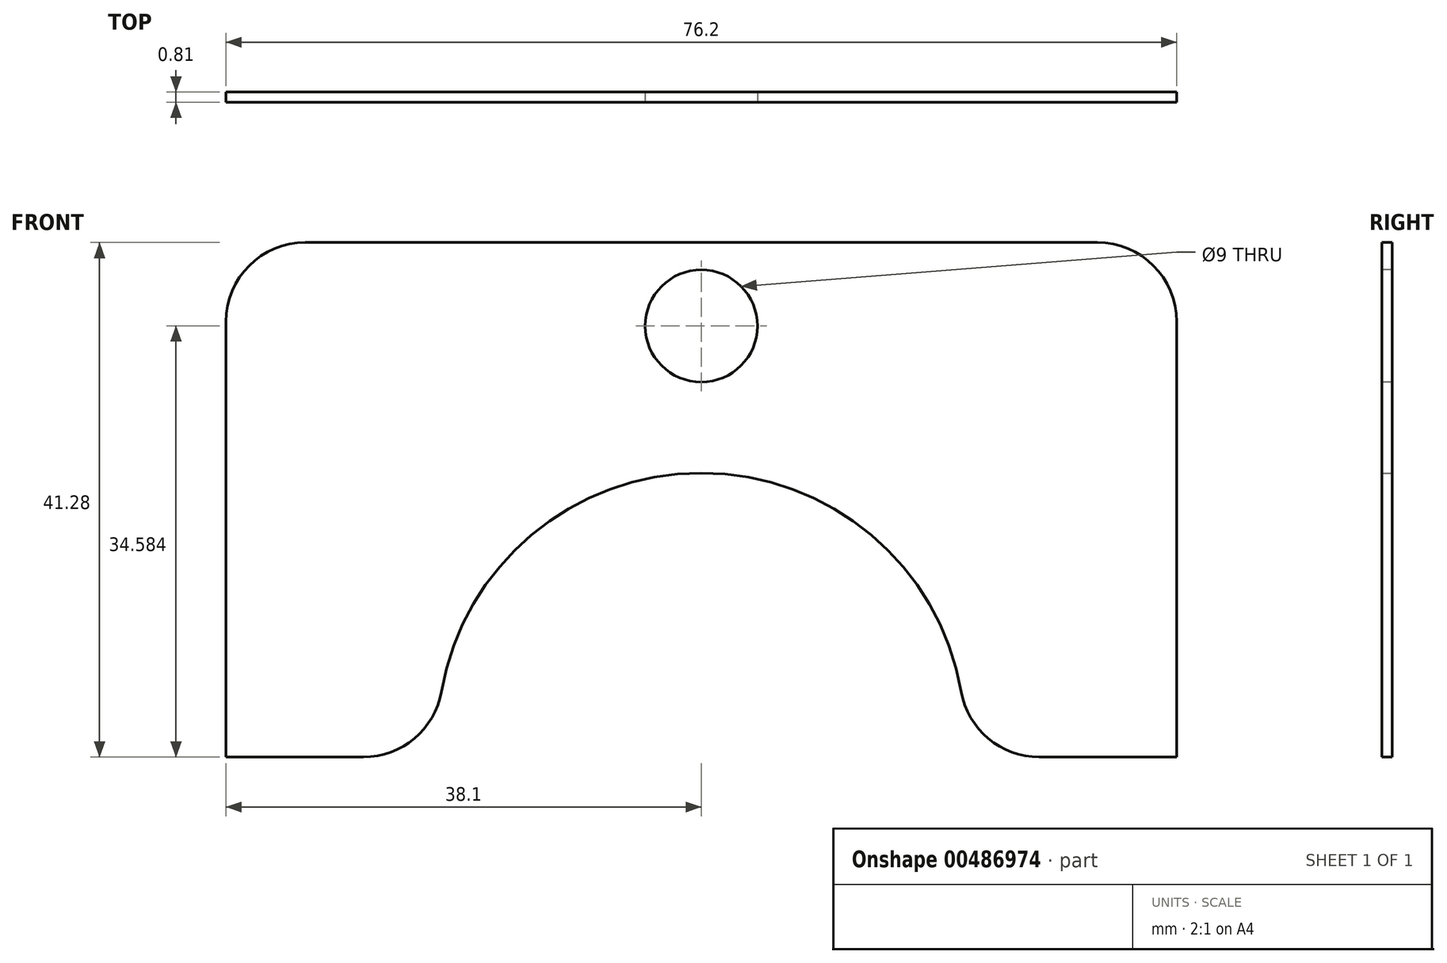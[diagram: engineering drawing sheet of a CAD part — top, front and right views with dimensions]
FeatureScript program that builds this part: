
annotation { "Feature Type Name" : "Feature", "Feature Type Description" : "" }
export const myFeature = defineFeature(function(context is Context, id is Id, definition is map)
    precondition{}
    {
        {
            var Q0;
            Q0=qCreatedBy(makeId("Front.planeOp"),FACE);
            var sketch = newSketch(context, id + "F0", { "sketchPlane" : qUnion([Q0])});
            skArc(sketch, "E0", {"start": v(20.83, 3.62) * mm, "mid": v(0, 21.15) * mm, "end": v(-20.83, 3.62) * mm});
            skLineSegment(sketch, "E1.bottom", {"start": v(-38.1, -1.64) * mm, "end": v(-27.09, -1.64) * mm});
            skLineSegment(sketch, "E1.top", {"start": v(-31.75, 39.64) * mm, "end": v(31.75, 39.64) * mm});
            skLineSegment(sketch, "E1.left", {"start": v(-38.1, -1.64) * mm, "end": v(-38.1, 33.29) * mm});
            skLineSegment(sketch, "E1.right", {"start": v(38.1, -1.64) * mm, "end": v(38.1, 33.29) * mm});
            skLineSegment(sketch, "E2.trimOffspring", {"start": v(27.09, -1.64) * mm, "end": v(38.1, -1.64) * mm});
            skPoint(sketch, "E3.visualSharp", {"position": v(21.08, -1.64) * mm});
            skArc(sketch, "E3.filletArc", {"start": v(20.83, 3.62) * mm, "mid": v(23, -0.15) * mm, "end": v(27.09, -1.64) * mm});
            skPoint(sketch, "E4.visualSharp", {"position": v(-21.08, -1.64) * mm});
            skArc(sketch, "E4.filletArc", {"start": v(-27.09, -1.64) * mm, "mid": v(-23, -0.15) * mm, "end": v(-20.83, 3.62) * mm});
            skPoint(sketch, "E5.visualSharp", {"position": v(-38.1, 39.64) * mm});
            skArc(sketch, "E5.filletArc", {"start": v(-31.75, 39.64) * mm, "mid": v(-36.24, 37.78) * mm, "end": v(-38.1, 33.29) * mm});
            skPoint(sketch, "E6.visualSharp", {"position": v(38.1, 39.64) * mm});
            skArc(sketch, "E6.filletArc", {"start": v(38.1, 33.29) * mm, "mid": v(36.24, 37.78) * mm, "end": v(31.75, 39.64) * mm});
            skSolve(sketch);
        }
        {
            var Q0;
            Q0=makeQuery(id+"F0.imprint","IMPRINT",FACE,{"disambiguationData":[TD([[makeQuery(id+"F0.imprint","IMPRINT",EDGE,{"derivedFrom":sQuery(id+"F0.wireOp",EDGE,"E0")}),-1.0]])]});
            extrude(context, id + "F1", {"entities" : qUnion([Q0]), "depth" : 0.81 * mm});
        }
        {
            var Q0;
            Q0=makeQuery(id+"F1.opExtrude","CAP_FACE",FACE,{"disambiguationData":[OSD([sQuery(id+"F0.wireOp",EDGE,"E0"),sQuery(id+"F0.wireOp",EDGE,"E1.bottom"),sQuery(id+"F0.wireOp",EDGE,"E1.top"),sQuery(id+"F0.wireOp",EDGE,"E1.left"),sQuery(id+"F0.wireOp",EDGE,"E1.right"),sQuery(id+"F0.wireOp",EDGE,"E2.trimOffspring"),sQuery(id+"F0.wireOp",EDGE,"E3.filletArc"),sQuery(id+"F0.wireOp",EDGE,"E4.filletArc")])],"isStart":false});
            var sketch = newSketch(context, id + "F2", { "sketchPlane" : qUnion([Q0])});
            skPoint(sketch, "E7", {"position": v(0, 32.94) * mm});
            skPoint(sketch, "E7.positionSnap0", {"position": v(0, 39.64) * mm});
            skCircle(sketch, "E8", {"center": v(0, 32.94) * mm, "radius": 4.5 * mm});
            skSolve(sketch);
        }
        {
            var Q0;
            Q0=makeQuery(id+"F2.imprint","IMPRINT",FACE,{"disambiguationData":[TD([[makeQuery(id+"F2.imprint","IMPRINT",EDGE,{"derivedFrom":sQuery(id+"F2.wireOp",EDGE,"E8")}),1.0]])]});
            extrude(context, id + "F3", {"entities" : qUnion([Q0]), "operationType" : NewBodyOperationType.REMOVE, "oppositeDirection" : true, "depth" : 25.4 * mm});
        }
    });
